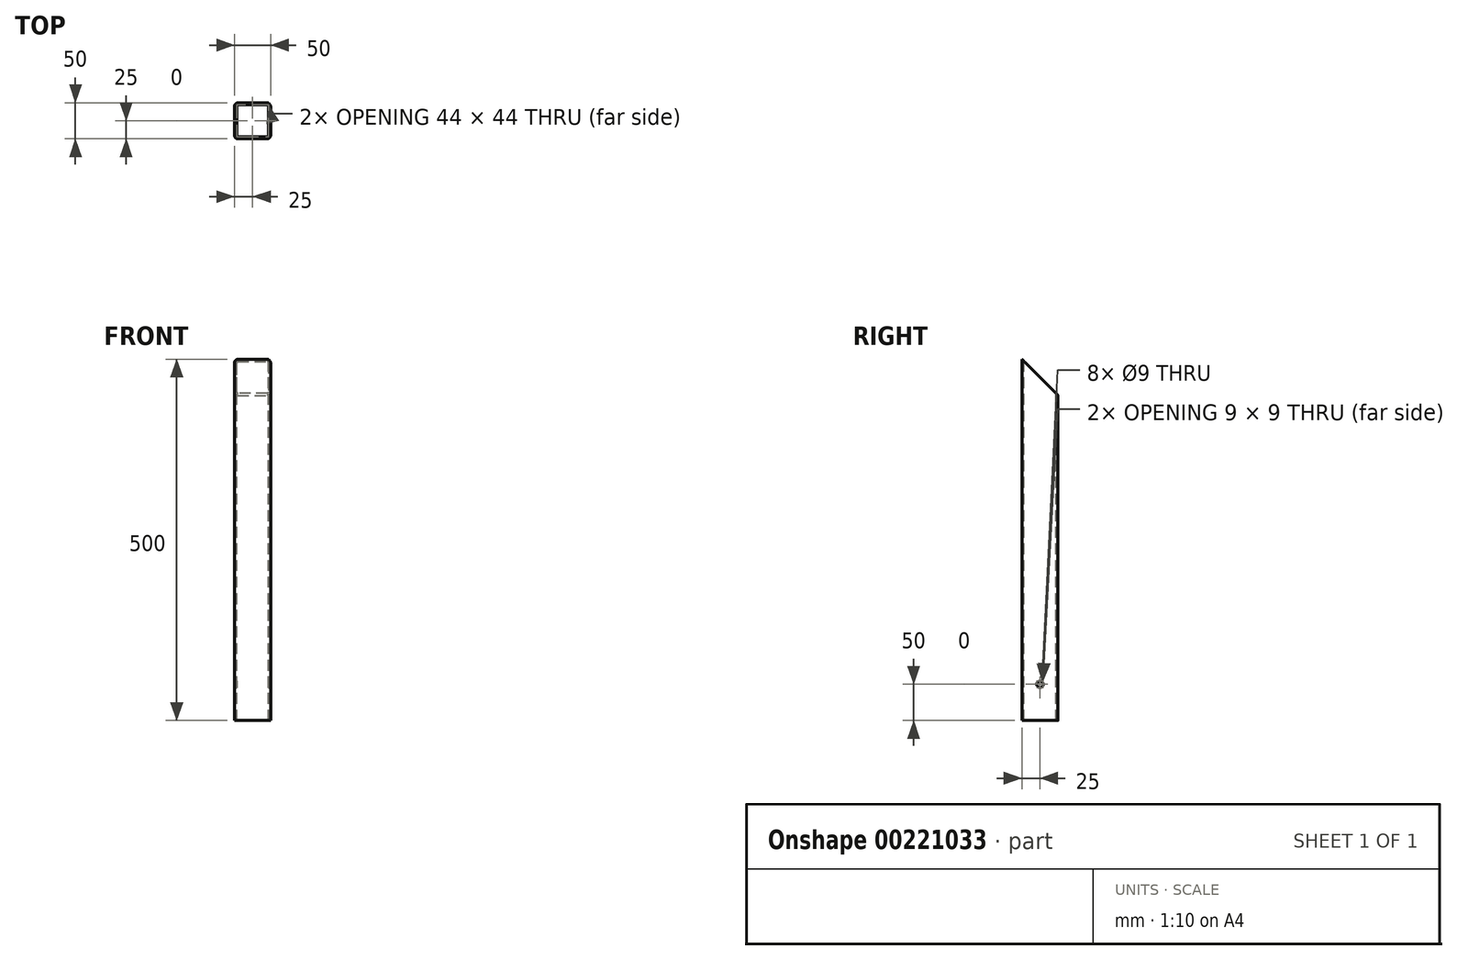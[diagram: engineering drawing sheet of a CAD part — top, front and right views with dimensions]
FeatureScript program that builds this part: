
annotation { "Feature Type Name" : "Feature", "Feature Type Description" : "" }
export const myFeature = defineFeature(function(context is Context, id is Id, definition is map)
    precondition{}
    {
        {
            var Q0;
            Q0=qCreatedBy(makeId("Top.planeOp"),FACE);
            var sketch = newSketch(context, id + "F0", { "sketchPlane" : qUnion([Q0])});
            skLineSegment(sketch, "E0.bottom", {"start": v(20, 25) * mm, "end": v(-20, 25) * mm});
            skLineSegment(sketch, "E0.top", {"start": v(20, -25) * mm, "end": v(-20, -25) * mm});
            skLineSegment(sketch, "E0.left", {"start": v(25, 20) * mm, "end": v(25, -20) * mm});
            skLineSegment(sketch, "E0.right", {"start": v(-25, 20) * mm, "end": v(-25, -20) * mm});
            skPoint(sketch, "E0.middle", {"position": v(0, 0) * mm});
            skPoint(sketch, "E1.visualSharp", {"position": v(25, -25) * mm});
            skArc(sketch, "E1.filletArc", {"start": v(20, -25) * mm, "mid": v(23.54, -23.54) * mm, "end": v(25, -20) * mm});
            skPoint(sketch, "E2.visualSharp", {"position": v(-25, -25) * mm});
            skArc(sketch, "E2.filletArc", {"start": v(-25, -20) * mm, "mid": v(-23.54, -23.54) * mm, "end": v(-20, -25) * mm});
            skPoint(sketch, "E3.visualSharp", {"position": v(-25, 25) * mm});
            skArc(sketch, "E3.filletArc", {"start": v(-20, 25) * mm, "mid": v(-23.54, 23.54) * mm, "end": v(-25, 20) * mm});
            skPoint(sketch, "E4.visualSharp", {"position": v(25, 25) * mm});
            skArc(sketch, "E4.filletArc", {"start": v(25, 20) * mm, "mid": v(23.54, 23.54) * mm, "end": v(20, 25) * mm});
            skSolve(sketch);
        }
        {
            var Q0;
            Q0=makeQuery(id+"F0.imprint","IMPRINT",FACE,{"disambiguationData":[TD([[makeQuery(id+"F0.imprint","IMPRINT",EDGE,{"derivedFrom":sQuery(id+"F0.wireOp",EDGE,"E0.bottom")}),1.0]])]});
            extrude(context, id + "F1", {"entities" : qUnion([Q0]), "depth" : 500 * mm});
        }
        {
            var Q0;
            Q0=makeQuery(id+"F1.opExtrude","CAP_FACE",FACE,{"disambiguationData":[OSD([sQuery(id+"F0.wireOp",EDGE,"E0.bottom"),sQuery(id+"F0.wireOp",EDGE,"E0.top"),sQuery(id+"F0.wireOp",EDGE,"E0.left"),sQuery(id+"F0.wireOp",EDGE,"E0.right"),sQuery(id+"F0.wireOp",EDGE,"E1.filletArc"),sQuery(id+"F0.wireOp",EDGE,"E2.filletArc"),sQuery(id+"F0.wireOp",EDGE,"E3.filletArc"),sQuery(id+"F0.wireOp",EDGE,"E4.filletArc")])],"isStart":false});
            var sketch = newSketch(context, id + "F2", { "sketchPlane" : qUnion([Q0])});
            skLineSegment(sketch, "E5.0", {"start": v(-20, -22) * mm, "end": v(20, -22) * mm});
            skLineSegment(sketch, "E5.1", {"start": v(-22, 20) * mm, "end": v(-22, -20) * mm});
            skLineSegment(sketch, "E5.2", {"start": v(20, 22) * mm, "end": v(-20, 22) * mm});
            skLineSegment(sketch, "E5.3", {"start": v(22, -20) * mm, "end": v(22, 20) * mm});
            skPoint(sketch, "E6.visualSharp", {"position": v(-22, -22) * mm});
            skArc(sketch, "E6.filletArc", {"start": v(-22, -20) * mm, "mid": v(-21.41, -21.41) * mm, "end": v(-20, -22) * mm});
            skPoint(sketch, "E7.visualSharp", {"position": v(22, -22) * mm});
            skArc(sketch, "E7.filletArc", {"start": v(20, -22) * mm, "mid": v(21.41, -21.41) * mm, "end": v(22, -20) * mm});
            skPoint(sketch, "E8.visualSharp", {"position": v(22, 22) * mm});
            skArc(sketch, "E8.filletArc", {"start": v(22, 20) * mm, "mid": v(21.41, 21.41) * mm, "end": v(20, 22) * mm});
            skPoint(sketch, "E9.visualSharp", {"position": v(-22, 22) * mm});
            skArc(sketch, "E9.filletArc", {"start": v(-20, 22) * mm, "mid": v(-21.41, 21.41) * mm, "end": v(-22, 20) * mm});
            skSolve(sketch);
        }
        {
            var Q0;
            Q0=makeQuery(id+"F2.imprint","IMPRINT",FACE,{"disambiguationData":[TD([[makeQuery(id+"F2.imprint","IMPRINT",EDGE,{"derivedFrom":sQuery(id+"F2.wireOp",EDGE,"E5.0")}),1.0]])]});
            extrude(context, id + "F3", {"entities" : qUnion([Q0]), "operationType" : NewBodyOperationType.REMOVE, "endBound" : BoundingType.THROUGH_ALL, "oppositeDirection" : true, "depth" : 25 * mm});
        }
        {
            var Q0;
            Q0=qCreatedBy(makeId("Right.planeOp"),FACE);
            var sketch = newSketch(context, id + "F4", { "sketchPlane" : qUnion([Q0])});
            skLineSegment(sketch, "E10", {"start": v(-25, 500) * mm, "end": v(25, 450) * mm});
            skLineSegment(sketch, "E11", {"start": v(25, 450) * mm, "end": v(25, 500) * mm});
            skLineSegment(sketch, "E12", {"start": v(25, 500) * mm, "end": v(-25, 500) * mm});
            skSolve(sketch);
        }
        {
            var Q0;
            Q0=qSketchRegion(id+"F4",true);
            extrude(context, id + "F5", {"entities" : qUnion([Q0]), "operationType" : NewBodyOperationType.REMOVE, "endBound" : BoundingType.THROUGH_ALL, "oppositeDirection" : true, "depth" : 25 * mm, "hasSecondDirection" : true, "secondDirectionOppositeDirection" : false, "secondDirectionDepth" : 25 * mm});
        }
        {
            var Q0;
            Q0=makeQuery(id+"F1.opExtrude","SWEPT_FACE",FACE,{"disambiguationData":[OSD([sQuery(id+"F0.wireOp",EDGE,"E0.left")])]});
            var sketch = newSketch(context, id + "F6", { "sketchPlane" : qUnion([Q0])});
            skPoint(sketch, "E13", {"position": v(0, 50) * mm});
            skSolve(sketch);
        }
        {
            var Q0;
            Q0=sQuery(id+"F6.wireOp",VERTEX,"E13");
            var Q1;
            Q1=makeQuery(id+"F1.opExtrude","SWEPT_BODY",BODY,{"disambiguationData":[OSD([sQuery(id+"F0.wireOp",EDGE,"E0.bottom"),sQuery(id+"F0.wireOp",EDGE,"E0.top"),sQuery(id+"F0.wireOp",EDGE,"E0.left"),sQuery(id+"F0.wireOp",EDGE,"E0.right"),sQuery(id+"F0.wireOp",EDGE,"E1.filletArc"),sQuery(id+"F0.wireOp",EDGE,"E2.filletArc"),sQuery(id+"F0.wireOp",EDGE,"E3.filletArc"),sQuery(id+"F0.wireOp",EDGE,"E4.filletArc")])]});
            hole(context, id + "F7", {"style" : HoleStyle.SIMPLE, "endStyle" : HoleEndStyle.THROUGH, "holeDiameter" : 9 * mm, "locations" : qUnion([Q0]), "scope" : qUnion([Q1]), "isTappedThrough" : true});
        }
    });
